# Revit family: DOME-S-KR-14800-840-MPS-DA
name_source: partatom
category: Leuchten
units: mm (PartAtom-declared; Revit-internal decimal feet)

## family parameters
Basisbauteil = Fläche
Beim Laden mit Abzugskörper schneiden = Nein
Bemaßung runder Anschluss = Durchmesser verwenden
Gemeinsam genutzt = Nein
Lichtquelle = Ja
OmniClass-Nummer = 23.80.70.11
OmniClass-Titel = Luminaries for Internal Lighting
Raumberechnungspunkt = Nein
Teiletyp = Normal

## types (1)
- DOME-S-KR-14800-840-MPS-DA
    Baugruppenkennzeichen = D5020200
    Datei für fotometrisches Netz = DOME-S-KG 14800-840 MPS-DA.IES
    Emissionsform beim Rendern sichtbar = Nein
    Farbfilter = 16777215
    Farbtemperaturverschiebung bei Dämpfen der Lampe = <Keine Auswahl>
    Hersteller = RIDI Leuchten GmbH
    Lampe = LED
    Modell = SPG0630175
    Neigungswinkel = 90.00°
    Scheinlast = 90 VA
    URL = https://www.spectral-lighting.com
    Von Breite des Rechtecks ausssenden = 251 mm  [stored 0.823491 ft]
    Von Länge des Rechtecks aussenden = 581 mm  [stored 1.90617 ft]
    Vorgabe-Ansicht = 0 mm  [stored 0 ft]
    brand = Spectral
    conformity mark = CE
    electrical safety class = 1
    height = 1945 mm  [stored 6.38123 ft]
    ingress protection (IP) code = IP20
    length = 499 mm  [stored 1.63714 ft]
    nominal frequency = 50-60Hz
    nominal voltage = 230
    product name = DOME-S-KR-14800-840-MPS-DA
    rated input power = 90
    voltage type (AC, DC, UC) = AC
    weight = 27.2 kg
    width = 680 mm  [stored 2.23097 ft]

note: [stored X ft] marks values corroborated as IEEE doubles in the binary element streams (Revit-internal decimal feet)
